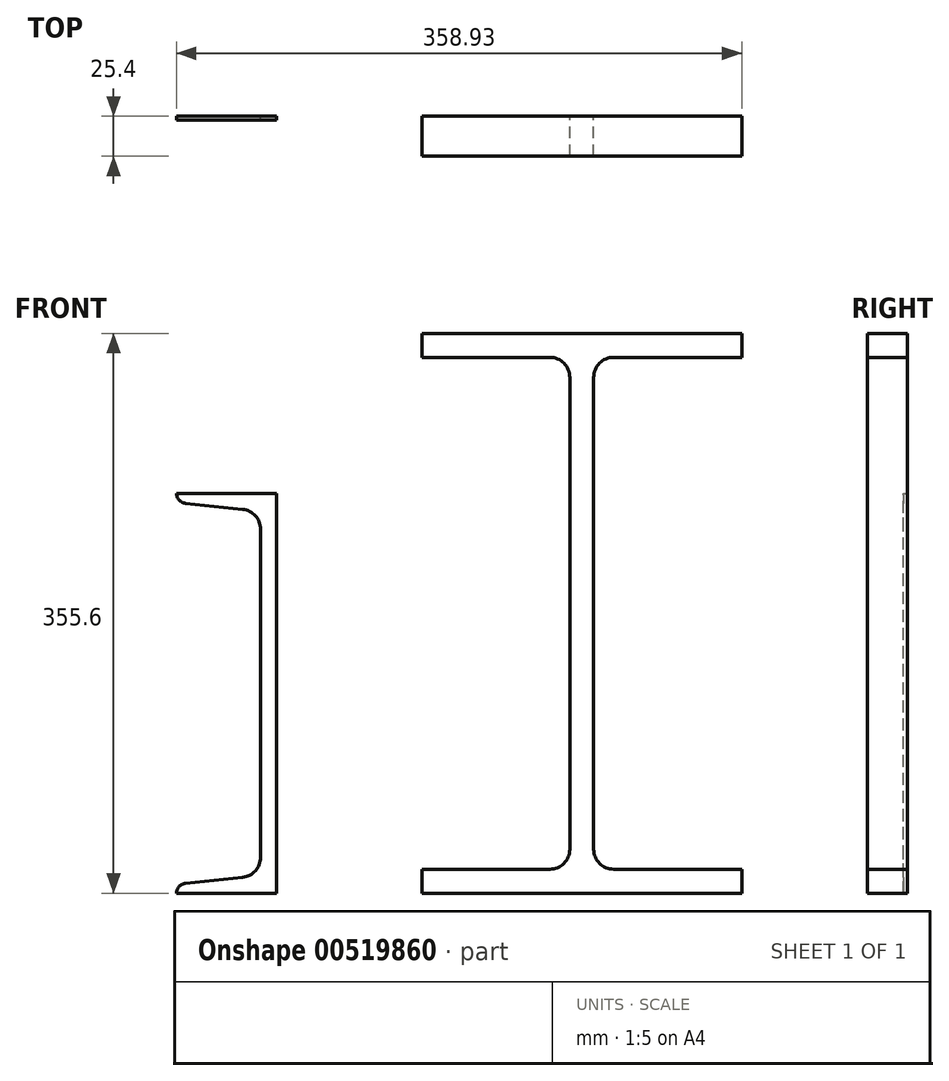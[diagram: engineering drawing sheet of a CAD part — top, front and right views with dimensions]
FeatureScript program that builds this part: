
annotation { "Feature Type Name" : "Feature", "Feature Type Description" : "" }
export const myFeature = defineFeature(function(context is Context, id is Id, definition is map)
    precondition{}
    {
        {
            var Q0;
            Q0=qCreatedBy(makeId("Front.planeOp"),FACE);
            var sketch = newSketch(context, id + "F0", { "sketchPlane" : qUnion([Q0])});
            skLineSegment(sketch, "E0.bottom", {"start": v(-101.6, 0) * mm, "end": v(0, 0) * mm});
            skLineSegment(sketch, "E0.top", {"start": v(-101.6, 15.24) * mm, "end": v(-20.32, 15.24) * mm});
            skLineSegment(sketch, "E0.left", {"start": v(-101.6, 0) * mm, "end": v(-101.6, 15.24) * mm});
            skLineSegment(sketch, "E0.right", {"start": v(0, 0) * mm, "end": v(0, 355.6) * mm, "construction": true});
            skLineSegment(sketch, "E1.right", {"start": v(-7.62, 27.94) * mm, "end": v(-7.62, 327.66) * mm});
            skLineSegment(sketch, "E2.bottom", {"start": v(-101.6, 355.6) * mm, "end": v(0, 355.6) * mm});
            skLineSegment(sketch, "E2.top", {"start": v(-101.6, 340.36) * mm, "end": v(-20.32, 340.36) * mm});
            skLineSegment(sketch, "E2.left", {"start": v(-101.6, 355.6) * mm, "end": v(-101.6, 340.36) * mm});
            skLineSegment(sketch, "E3.MirrorCS", {"start": v(101.6, 0) * mm, "end": v(101.6, 15.24) * mm});
            skLineSegment(sketch, "E4.MirrorCS", {"start": v(7.62, 27.94) * mm, "end": v(7.62, 327.66) * mm});
            skLineSegment(sketch, "E5.MirrorCS", {"start": v(101.6, 340.36) * mm, "end": v(20.32, 340.36) * mm});
            skLineSegment(sketch, "E6.MirrorCS", {"start": v(101.6, 15.24) * mm, "end": v(20.32, 15.24) * mm});
            skLineSegment(sketch, "E7.MirrorCS", {"start": v(101.6, 355.6) * mm, "end": v(101.6, 340.36) * mm});
            skLineSegment(sketch, "E8.MirrorCS", {"start": v(101.6, 355.6) * mm, "end": v(0, 355.6) * mm});
            skLineSegment(sketch, "E9.MirrorCS", {"start": v(101.6, 0) * mm, "end": v(0, 0) * mm});
            skPoint(sketch, "E10.visualSharp", {"position": v(7.62, 340.36) * mm});
            skArc(sketch, "E10.filletArc", {"start": v(20.32, 340.36) * mm, "mid": v(11.34, 336.64) * mm, "end": v(7.62, 327.66) * mm});
            skPoint(sketch, "E11.visualSharp", {"position": v(-7.62, 340.36) * mm});
            skArc(sketch, "E11.filletArc", {"start": v(-7.62, 327.66) * mm, "mid": v(-11.34, 336.64) * mm, "end": v(-20.32, 340.36) * mm});
            skPoint(sketch, "E12.visualSharp", {"position": v(-7.62, 15.24) * mm});
            skArc(sketch, "E12.filletArc", {"start": v(-20.32, 15.24) * mm, "mid": v(-11.34, 18.96) * mm, "end": v(-7.62, 27.94) * mm});
            skPoint(sketch, "E13.visualSharp", {"position": v(7.62, 15.24) * mm});
            skArc(sketch, "E13.filletArc", {"start": v(7.62, 27.94) * mm, "mid": v(11.34, 18.96) * mm, "end": v(20.32, 15.24) * mm});
            skSolve(sketch);
        }
        {
            var Q0;
            Q0=makeQuery(id+"F0.imprint","IMPRINT",FACE,{"disambiguationData":[TD([[makeQuery(id+"F0.imprint","IMPRINT",EDGE,{"derivedFrom":sQuery(id+"F0.wireOp",EDGE,"E0.bottom")}),1.0]])]});
            extrude(context, id + "F1", {"entities" : qUnion([Q0]), "depth" : 25.4 * mm, "offsetDistance" : 25.4 * mm});
        }
        {
            var Q0;
            Q0=qCreatedBy(makeId("Front.planeOp"),FACE);
            var sketch = newSketch(context, id + "F2", { "sketchPlane" : qUnion([Q0])});
            skLineSegment(sketch, "E14.top", {"start": v(-193.83, 127) * mm, "end": v(-204, 127) * mm});
            skLineSegment(sketch, "E14.left", {"start": v(-193.83, 0) * mm, "end": v(-193.83, 127) * mm});
            skLineSegment(sketch, "E14.right", {"start": v(-204, 22.76) * mm, "end": v(-204, 127) * mm});
            skLineSegment(sketch, "E15", {"start": v(-215.36, 10.13) * mm, "end": v(-251.64, 6.32) * mm});
            skLineSegment(sketch, "E16", {"start": v(-193.83, 0) * mm, "end": v(-257.33, 0) * mm});
            skLineSegment(sketch, "E17", {"start": v(-130.55, 127) * mm, "end": v(-266.63, 127) * mm, "construction": true});
            skArc(sketch, "E18", {"start": v(-251.64, 6.32) * mm, "mid": v(-255.7, 4.25) * mm, "end": v(-257.33, 0) * mm});
            skPoint(sketch, "E19.start.orphan", {"position": v(-257.33, 5.72) * mm});
            skPoint(sketch, "E20.visualSharp", {"position": v(-204, 11.32) * mm});
            skArc(sketch, "E20.filletArc", {"start": v(-215.36, 10.13) * mm, "mid": v(-207.25, 14.26) * mm, "end": v(-204, 22.76) * mm});
            skArc(sketch, "E21.MirrorCS", {"start": v(-215.36, 243.87) * mm, "mid": v(-207.25, 239.74) * mm, "end": v(-204, 231.24) * mm});
            skArc(sketch, "E22.MirrorCS", {"start": v(-251.64, 247.68) * mm, "mid": v(-255.7, 249.75) * mm, "end": v(-257.33, 254) * mm});
            skLineSegment(sketch, "E23.MirrorCS", {"start": v(-215.36, 243.87) * mm, "end": v(-251.64, 247.68) * mm});
            skLineSegment(sketch, "E24.MirrorCS", {"start": v(-193.83, 254) * mm, "end": v(-193.83, 127) * mm});
            skPoint(sketch, "E25.MirrorP", {"position": v(-204, 242.68) * mm});
            skLineSegment(sketch, "E26.MirrorCS", {"start": v(-204, 231.24) * mm, "end": v(-204, 127) * mm});
            skPoint(sketch, "E27.MirrorP", {"position": v(-257.33, 248.28) * mm});
            skLineSegment(sketch, "E28.MirrorCS", {"start": v(-193.83, 254) * mm, "end": v(-257.33, 254) * mm});
            skSolve(sketch);
        }
        {
            var Q0;
            Q0 = qSketchRegion(id + "F2", true);
            extrude(context, id + "F3", {"entities" : qUnion([Q0]), "depth" : 2.54 * mm, "offsetDistance" : 25.4 * mm});
        }
    });
